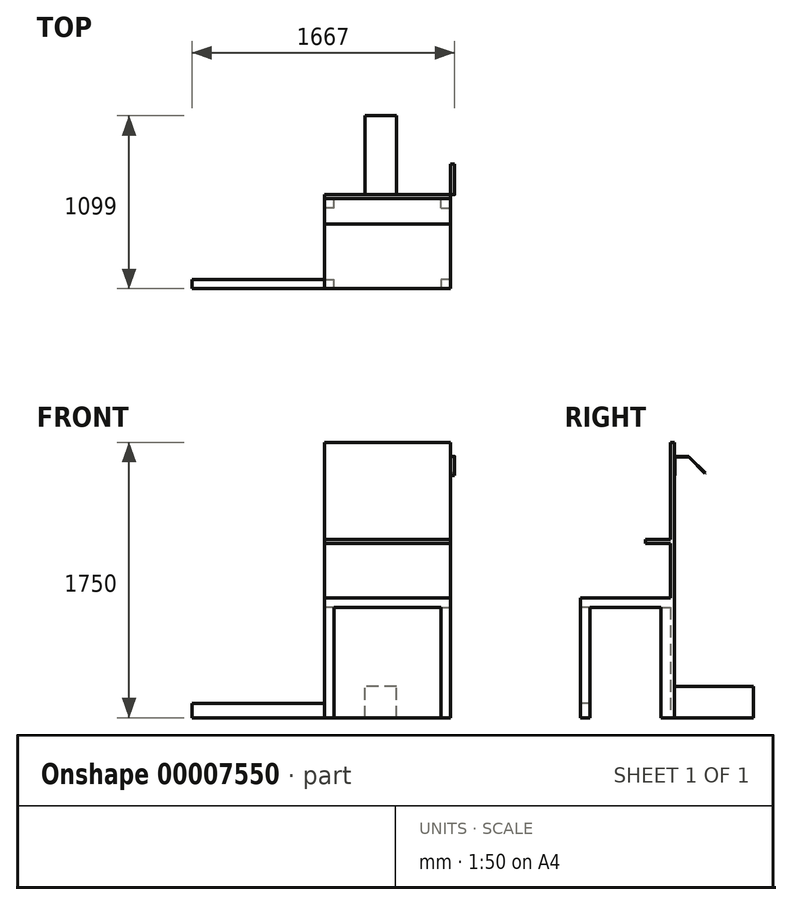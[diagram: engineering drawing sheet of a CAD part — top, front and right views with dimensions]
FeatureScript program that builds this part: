
annotation { "Feature Type Name" : "Feature", "Feature Type Description" : "" }
export const myFeature = defineFeature(function(context is Context, id is Id, definition is map)
    precondition{}
    {
        {
            var Q0;
            Q0=qCreatedBy(makeId("Front.planeOp"),FACE);
            var sketch = newSketch(context, id + "F0", { "sketchPlane" : qUnion([Q0])});
            skLineSegment(sketch, "E0.bottom", {"start": v(-800, 1750) * mm, "end": v(0, 1750) * mm});
            skLineSegment(sketch, "E0.top", {"start": v(-800, 0) * mm, "end": v(0, 0) * mm});
            skLineSegment(sketch, "E0.left", {"start": v(-800, 1750) * mm, "end": v(-800, 0) * mm});
            skLineSegment(sketch, "E0.right", {"start": v(0, 1750) * mm, "end": v(0, 0) * mm});
            skSolve(sketch);
        }
        {
            var Q0;
            Q0=makeQuery(id+"F0.imprint","IMPRINT",FACE,{"disambiguationData":[TD([[makeQuery(id+"F0.imprint","IMPRINT",EDGE,{"derivedFrom":sQuery(id+"F0.wireOp",EDGE,"E0.bottom")}),-1.0]])]});
            extrude(context, id + "F1", {"entities" : qUnion([Q0]), "depth" : 25 * mm});
        }
        {
            var Q0;
            Q0=qCreatedBy(makeId("Top.planeOp"),FACE);
            var sketch = newSketch(context, id + "F2", { "sketchPlane" : qUnion([Q0])});
            skLineSegment(sketch, "E1.bottom", {"start": v(-740, -85) * mm, "end": v(-800, -85) * mm});
            skLineSegment(sketch, "E1.top", {"start": v(-740, -25) * mm, "end": v(-800, -25) * mm});
            skLineSegment(sketch, "E1.left", {"start": v(-740, -85) * mm, "end": v(-740, -25) * mm});
            skLineSegment(sketch, "E1.right", {"start": v(-800, -85) * mm, "end": v(-800, -25) * mm});
            skLineSegment(sketch, "E2.bottom", {"start": v(-60, -85) * mm, "end": v(0, -85) * mm});
            skLineSegment(sketch, "E2.top", {"start": v(-60, -25) * mm, "end": v(0, -25) * mm});
            skLineSegment(sketch, "E2.left", {"start": v(-60, -85) * mm, "end": v(-60, -25) * mm});
            skLineSegment(sketch, "E2.right", {"start": v(0, -85) * mm, "end": v(0, -25) * mm});
            skLineSegment(sketch, "E3.bottom", {"start": v(0, -537) * mm, "end": v(-60, -537) * mm});
            skLineSegment(sketch, "E3.top", {"start": v(0, -597) * mm, "end": v(-60, -597) * mm});
            skLineSegment(sketch, "E3.left", {"start": v(0, -537) * mm, "end": v(0, -597) * mm});
            skLineSegment(sketch, "E3.right", {"start": v(-60, -537) * mm, "end": v(-60, -597) * mm});
            skLineSegment(sketch, "E4.bottom", {"start": v(-800, -597) * mm, "end": v(-740, -597) * mm});
            skLineSegment(sketch, "E4.top", {"start": v(-800, -537) * mm, "end": v(-740, -537) * mm});
            skLineSegment(sketch, "E4.left", {"start": v(-800, -597) * mm, "end": v(-800, -537) * mm});
            skLineSegment(sketch, "E4.right", {"start": v(-740, -597) * mm, "end": v(-740, -537) * mm});
            skSolve(sketch);
        }
        {
            var Q0;
            Q0 = qSketchRegion(id + "F2", true);
            extrude(context, id + "F3", {"entities" : qUnion([Q0]), "depth" : 760 * mm});
        }
        {
            var Q0;
            Q0=makeQuery(id+"F3.opExtrude","CAP_FACE",FACE,{"disambiguationData":[OSD([sQuery(id+"F2.wireOp",EDGE,"E4.bottom"),sQuery(id+"F2.wireOp",EDGE,"E4.top"),sQuery(id+"F2.wireOp",EDGE,"E4.left"),sQuery(id+"F2.wireOp",EDGE,"E4.right")])],"isStart":false});
            var sketch = newSketch(context, id + "F4", { "sketchPlane" : qUnion([Q0])});
            skLineSegment(sketch, "E5.bottom", {"start": v(-800, -597) * mm, "end": v(0, -597) * mm});
            skLineSegment(sketch, "E5.top", {"start": v(-800, -25) * mm, "end": v(0, -25) * mm});
            skLineSegment(sketch, "E5.left", {"start": v(-800, -597) * mm, "end": v(-800, -25) * mm});
            skLineSegment(sketch, "E5.right", {"start": v(0, -597) * mm, "end": v(0, -25) * mm});
            skSolve(sketch);
        }
        {
            var Q0;
            Q0 = qSketchRegion(id + "F4", true);
            extrude(context, id + "F5", {"entities" : qUnion([Q0]), "operationType" : NewBodyOperationType.ADD, "oppositeDirection" : true, "depth" : 60 * mm});
        }
        {
            var Q0;
            Q0=makeQuery(id+"F1.opExtrude","CAP_FACE",FACE,{"disambiguationData":[OSD([sQuery(id+"F0.wireOp",EDGE,"E0.bottom"),sQuery(id+"F0.wireOp",EDGE,"E0.top"),sQuery(id+"F0.wireOp",EDGE,"E0.left"),sQuery(id+"F0.wireOp",EDGE,"E0.right")])],"isStart":true});
            var sketch = newSketch(context, id + "F6", { "sketchPlane" : qUnion([Q0])});
            skLineSegment(sketch, "E6.bottom", {"start": v(343.57, 0) * mm, "end": v(543.57, 0) * mm});
            skLineSegment(sketch, "E6.top", {"start": v(343.57, 200) * mm, "end": v(543.57, 200) * mm});
            skLineSegment(sketch, "E6.left", {"start": v(343.57, 0) * mm, "end": v(343.57, 200) * mm});
            skLineSegment(sketch, "E6.right", {"start": v(543.57, 0) * mm, "end": v(543.57, 200) * mm});
            skSolve(sketch);
        }
        {
            var Q0;
            Q0 = qSketchRegion(id + "F6", true);
            extrude(context, id + "F7", {"entities" : qUnion([Q0]), "depth" : 502 * mm});
        }
        {
            var Q0;
            Q0=makeQuery(id+"F5.boolean.opBoolean","MERGE",FACE,{"derivedFrom":[makeQuery(id+"F1.opExtrude","SWEPT_FACE",FACE,{"disambiguationData":[OSD([sQuery(id+"F0.wireOp",EDGE,"E0.left")])]}),makeQuery(id+"F3.opExtrude","SWEPT_FACE",FACE,{"disambiguationData":[OSD([sQuery(id+"F2.wireOp",EDGE,"E1.right")])]}),makeQuery(id+"F3.opExtrude","SWEPT_FACE",FACE,{"disambiguationData":[OSD([sQuery(id+"F2.wireOp",EDGE,"E4.left")])]}),makeQuery(id+"F5.opExtrude","SWEPT_FACE",FACE,{"disambiguationData":[OSD([sQuery(id+"F4.wireOp",EDGE,"E5.left")])]})]});
            var sketch = newSketch(context, id + "F8", { "sketchPlane" : qUnion([Q0])});
            skLineSegment(sketch, "E7.bottom", {"start": v(537, 0) * mm, "end": v(597, 0) * mm});
            skLineSegment(sketch, "E7.top", {"start": v(537, 90) * mm, "end": v(597, 90) * mm});
            skLineSegment(sketch, "E7.left", {"start": v(537, 0) * mm, "end": v(537, 90) * mm});
            skLineSegment(sketch, "E7.right", {"start": v(597, 0) * mm, "end": v(597, 90) * mm});
            skSolve(sketch);
        }
        {
            var Q0;
            Q0 = qSketchRegion(id + "F8", true);
            extrude(context, id + "F9", {"entities" : qUnion([Q0]), "depth" : 842 * mm});
        }
        {
            var Q0;
            {var subQ0=sQuery(id+"F0.wireOp",EDGE,"E0.bottom");var subQ1=sQuery(id+"F0.wireOp",EDGE,"E0.left");var subQ2=sQuery(id+"F0.wireOp",EDGE,"E0.right");Q0=makeQuery(id+"F5.boolean.opBoolean","SPLIT",FACE,{"disambiguationData":[TD([makeQuery(id+"F1.opExtrude","SWEPT_FACE",FACE,{"disambiguationData":[OSD([subQ0])]})])],"derivedFrom":makeQuery(id+"F1.opExtrude","CAP_FACE",FACE,{"disambiguationData":[OSD([subQ0,sQuery(id+"F0.wireOp",EDGE,"E0.top"),subQ1,subQ2])],"isStart":false})});}
            var sketch = newSketch(context, id + "F10", { "sketchPlane" : qUnion([Q0])});
            skLineSegment(sketch, "E8.bottom", {"start": v(-800, 1134) * mm, "end": v(0, 1134) * mm});
            skLineSegment(sketch, "E8.top", {"start": v(-800, 1106) * mm, "end": v(0, 1106) * mm});
            skLineSegment(sketch, "E8.left", {"start": v(-800, 1134) * mm, "end": v(-800, 1106) * mm});
            skLineSegment(sketch, "E8.right", {"start": v(0, 1134) * mm, "end": v(0, 1106) * mm});
            skSolve(sketch);
        }
        {
            var Q0;
            Q0=makeQuery(id+"F10.imprint","IMPRINT",FACE,{"disambiguationData":[TD([[makeQuery(id+"F10.imprint","IMPRINT",EDGE,{"derivedFrom":sQuery(id+"F10.wireOp",EDGE,"E8.bottom")}),-1.0]])]});
            extrude(context, id + "F11", {"entities" : qUnion([Q0]), "operationType" : NewBodyOperationType.ADD, "depth" : 160 * mm});
        }
        {
            var Q0;
            Q0=qCreatedBy(makeId("Right.planeOp"),FACE);
            var sketch = newSketch(context, id + "F12", { "sketchPlane" : qUnion([Q0])});
            skLineSegment(sketch, "E9", {"start": v(0, 1540) * mm, "end": v(0, 1649) * mm});
            skLineSegment(sketch, "E10", {"start": v(11, 1660) * mm, "end": v(85.44, 1660) * mm});
            skLineSegment(sketch, "E11", {"start": v(93.22, 1656.78) * mm, "end": v(196.07, 1553.93) * mm});
            skLineSegment(sketch, "E12", {"start": v(196.07, 1553.93) * mm, "end": v(194.65, 1552.52) * mm});
            skLineSegment(sketch, "E13", {"start": v(194.65, 1552.52) * mm, "end": v(91.8, 1655.36) * mm});
            skLineSegment(sketch, "E14", {"start": v(85.44, 1658) * mm, "end": v(11, 1658) * mm});
            skLineSegment(sketch, "E15", {"start": v(2, 1649) * mm, "end": v(2, 1540) * mm});
            skLineSegment(sketch, "E16", {"start": v(2, 1540) * mm, "end": v(0, 1540) * mm});
            skPoint(sketch, "E17.visualSharp", {"position": v(2, 1658) * mm});
            skArc(sketch, "E17.filletArc", {"start": v(11, 1658) * mm, "mid": v(4.64, 1655.36) * mm, "end": v(2, 1649) * mm});
            skPoint(sketch, "E18.visualSharp", {"position": v(89.17, 1658) * mm});
            skArc(sketch, "E18.filletArc", {"start": v(91.8, 1655.36) * mm, "mid": v(88.89, 1657.31) * mm, "end": v(85.44, 1658) * mm});
            skPoint(sketch, "E19.visualSharp", {"position": v(0, 1660) * mm});
            skArc(sketch, "E19.filletArc", {"start": v(11, 1660) * mm, "mid": v(3.22, 1656.78) * mm, "end": v(0, 1649) * mm});
            skPoint(sketch, "E20.visualSharp", {"position": v(90, 1660) * mm});
            skArc(sketch, "E20.filletArc", {"start": v(93.22, 1656.78) * mm, "mid": v(89.65, 1659.16) * mm, "end": v(85.44, 1660) * mm});
            skSolve(sketch);
        }
        {
            var Q0;
            Q0 = qSketchRegion(id + "F12", true);
            extrude(context, id + "F13", {"entities" : qUnion([Q0]), "depth" : 25 * mm});
        }
    });
